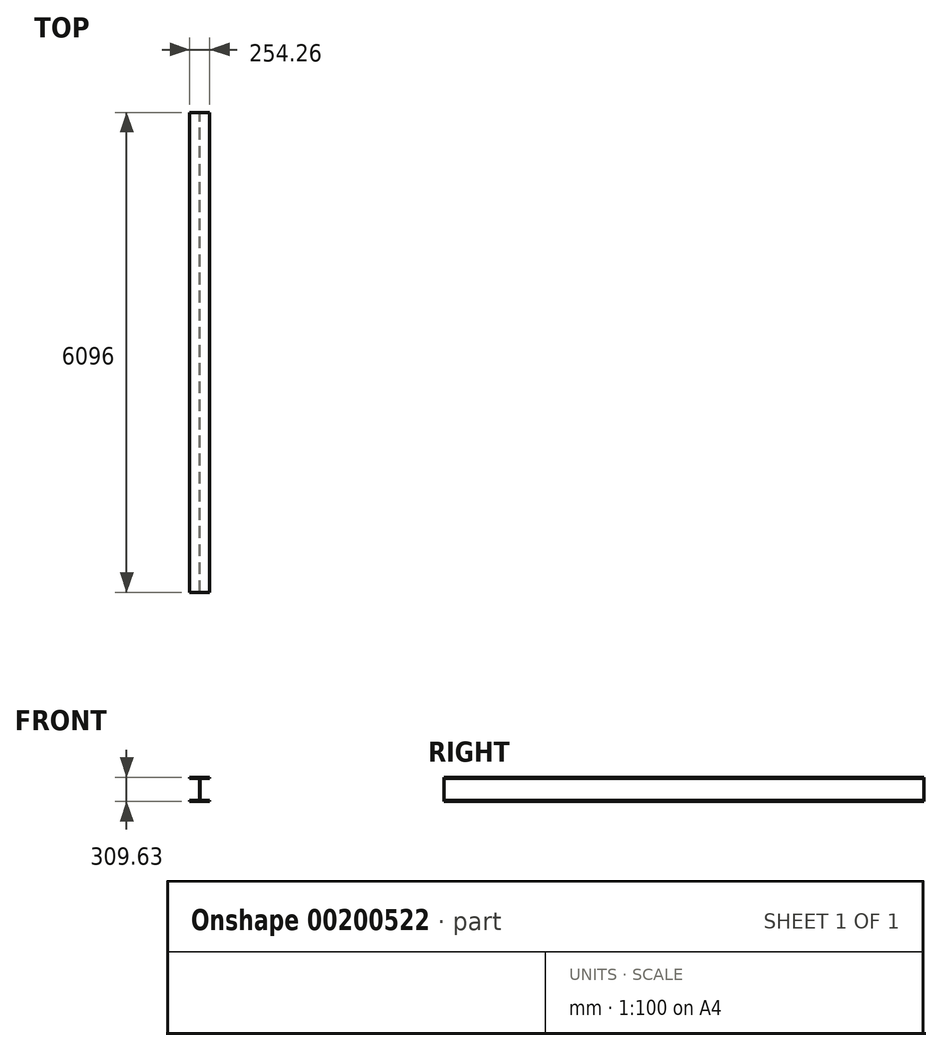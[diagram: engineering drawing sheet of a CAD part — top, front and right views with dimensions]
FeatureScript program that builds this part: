
annotation { "Feature Type Name" : "Feature", "Feature Type Description" : "" }
export const myFeature = defineFeature(function(context is Context, id is Id, definition is map)
    precondition{}
    {
        {
            var Q0;
            Q0=qCreatedBy(makeId("Front.planeOp"),FACE);
            var sketch = newSketch(context, id + "F0", { "sketchPlane" : qUnion([Q0])});
            skLineSegment(sketch, "E0", {"start": v(127.13, 0) * mm, "end": v(127.13, 16.26) * mm});
            skLineSegment(sketch, "E1", {"start": v(127.13, 16.26) * mm, "end": v(4.57, 16.26) * mm});
            skLineSegment(sketch, "E2", {"start": v(4.57, 16.26) * mm, "end": v(4.57, 293.37) * mm});
            skLineSegment(sketch, "E3", {"start": v(4.57, 293.37) * mm, "end": v(127.13, 293.37) * mm});
            skLineSegment(sketch, "E4", {"start": v(127.13, 293.37) * mm, "end": v(127.13, 309.63) * mm});
            skLineSegment(sketch, "E5", {"start": v(127.13, 309.63) * mm, "end": v(0, 309.63) * mm});
            skLineSegment(sketch, "E6", {"start": v(127.13, 0) * mm, "end": v(0, 0) * mm});
            skLineSegment(sketch, "E7", {"start": v(0, -24.07) * mm, "end": v(0, 108.97) * mm, "construction": true});
            skLineSegment(sketch, "E8.MirrorCS", {"start": v(-127.13, 293.37) * mm, "end": v(-127.13, 309.63) * mm});
            skLineSegment(sketch, "E9.MirrorCS", {"start": v(-127.13, 0) * mm, "end": v(-127.13, 16.26) * mm});
            skLineSegment(sketch, "E10.MirrorCS", {"start": v(-127.13, 16.26) * mm, "end": v(-4.57, 16.26) * mm});
            skLineSegment(sketch, "E11.MirrorCS", {"start": v(-4.57, 16.26) * mm, "end": v(-4.57, 293.37) * mm});
            skLineSegment(sketch, "E12.MirrorCS", {"start": v(-4.57, 293.37) * mm, "end": v(-127.13, 293.37) * mm});
            skLineSegment(sketch, "E13.MirrorCS", {"start": v(-127.13, 309.63) * mm, "end": v(0, 309.63) * mm});
            skLineSegment(sketch, "E14.MirrorCS", {"start": v(-127.13, 0) * mm, "end": v(0, 0) * mm});
            skSolve(sketch);
        }
        {
            var Q0;
            Q0=qSketchRegion(id+"F0",true);
            extrude(context, id + "F1", {"entities" : qUnion([Q0]), "depth" : 6096 * mm, "offsetDistance" : 25.4 * mm});
        }
    });
